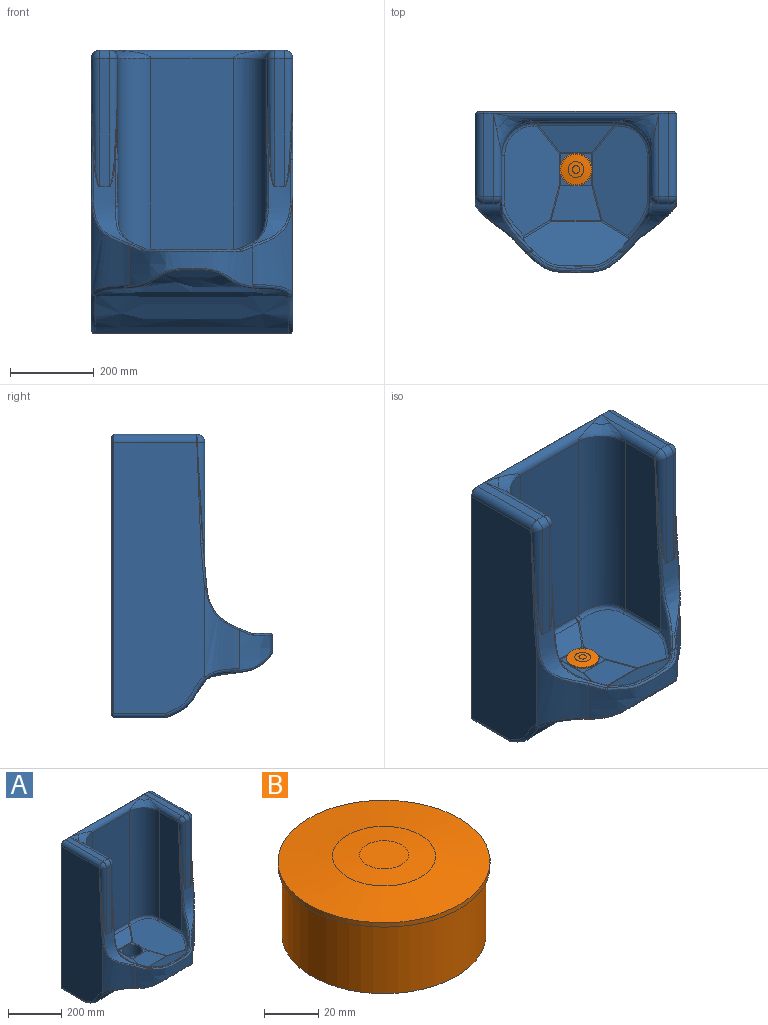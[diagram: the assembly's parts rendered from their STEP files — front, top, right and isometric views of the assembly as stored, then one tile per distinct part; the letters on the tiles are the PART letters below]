
ASSEMBLY  parts=2 mates=1
PART A: 140 faces, bbox 493.7x387.3x692.1 mm
  f0: bspline ~91.82x91.82mm, area 3088mm2, adj f69,f71,f137,f138
  f1: bspline ~91.82x91.82mm, area 3088mm2, adj f68,f69,f134,f135
  f2: plane 263.56x130.26mm, normal (0.24,0,0.97), area 28131.6mm2, adj f92,f97,f100,f101,f105,f106,f109,f110
  f3: plane 263.14x130.26mm, normal (-0.24,0,0.97), area 27983.2mm2, adj f85,f89,f90,f94,f95,f98,f99,f102
  f4: plane 199.28x23.5mm, normal (0,0,1), area 4683mm2, adj f71,f75,f80,f129
  f5: plane 463x125.22mm, normal (0,0,-1), area 57976mm2, adj f118,f120,f121,f130
  f6: plane 649.01x219.29mm, normal (1,0,0), area 134535.2mm2, adj f9,f33,f37,f80,f117,f118,f133
  f7: extruded ~308.32x96.53mm, area 21555.4mm2, adj f8,f9,f42,f45,f46,f47,f50,f116
  f8: extruded ~217.07x91.54mm, area 15555.5mm2, adj f7,f13,f34,f38,f42,f123,f124
  f9: extruded ~219.07x95.91mm, area 16070.7mm2, adj f6,f7,f37,f41,f45,f116,f117
  f10: plane 75.52x34.33mm, normal (0,0,1), area 647.8mm2, adj f81,f90,f91,f100
  f11: extruded ~215.89x127.47mm, area 8204.1mm2, adj f32,f36,f37,f40,f41,f45,f49,f53
  f12: extruded ~215.89x126.98mm, area 7962.1mm2, adj f31,f34,f35,f38,f39,f42,f48,f51
  f13: plane 649.01x219.29mm, normal (-1,0,0), area 134535.2mm2, adj f8,f30,f34,f59,f121,f123,f126
  f14: plane 228.61x44.47mm, normal (0,0,1), area 1469.2mm2, adj f46,f51,f54,f57
  f15: plane 305.81x23.5mm, normal (0,-1,0), area 7186.5mm2, adj f26,f29,f35,f63
  f16: plane 305.81x23.5mm, normal (0,-1,0), area 7186.5mm2, adj f27,f28,f36,f75
  f17: plane 199.28x23.5mm, normal (0,0,1), area 4683mm2, adj f59,f63,f68,f129
  f18: plane 489.87x121.03mm, normal (-1,0,0), area 54168.9mm2, adj f22,f44,f49,f53,f71,f94,f98,f138
  f19: plane 489.25x119.68mm, normal (1,0,0), area 54166.7mm2, adj f22,f43,f48,f52,f68,f101,f106,f135
  f20: plane 669x473mm, normal (0,1,0), area 316329.7mm2, adj f126,f127,f128,f129,f130,f131,f132,f133
  f21: plane 508.8x196.66mm, normal (0,-1,0), area 100045.2mm2, adj f69,f102,f110,f111,f135,f138
  f22: extruded ~356x149.3mm, area 21982mm2, adj f18,f19,f24,f25,f52,f53,f55,f56
  f23: plane 75.52x33.75mm, normal (0,0,1), area 603.7mm2, adj f81,f99,f108,f109
  f24: plane 58.7x1.71mm, normal (0,0,1), area 35.8mm2, adj f22,f25
  f25: plane 250.47x105.46mm, normal (0,0.38,0.92), area 21551.1mm2, adj f22,f24,f88,f89,f94,f97,f101
  f26: cylinder r=20mm len=305.81mm, axis (0,0,-1), area 4605.5mm2, adj f15,f39,f64
  f27: cylinder r=20mm len=305.81mm, axis (0,0,1), area 4605.5mm2, adj f16,f40,f74
  f28: cylinder r=20mm len=305.81mm, axis (0,0,-1), area 4605.5mm2, adj f16,f32,f76
  f29: cylinder r=20mm len=305.81mm, axis (0,0,-1), area 4605.5mm2, adj f15,f31,f62
  f30: bspline ~264.56x16.21mm, area 908mm2, adj f13,f31,f34,f58
  f31: bspline ~331.15x25.29mm, area 495.5mm2, adj f12,f29,f30,f35,f58,f61
  f32: bspline ~337.72x25.79mm, area 495.5mm2, adj f11,f28,f33,f36,f77,f78
  f33: bspline ~260.8x15.67mm, area 908mm2, adj f6,f32,f37,f78
  f34: bspline ~158.45x18.65mm, area 824.3mm2, adj f8,f12,f13,f30,f38
  f35: cylinder r=5mm len=23.5mm, axis (-1,0,0), area 9mm2, adj f12,f15,f31,f39
  f36: cylinder r=5mm len=23.5mm, axis (-1,0,0), area 9mm2, adj f11,f16,f32,f40
  f37: bspline ~158.45x18.65mm, area 816.4mm2, adj f6,f9,f11,f33,f41
  f38: bspline ~111.33x98.62mm, area 905.9mm2, adj f8,f12,f34,f42
  f39: bspline ~337.72x25.79mm, area 495.5mm2, adj f12,f26,f35,f43,f65,f66
  f40: bspline ~331.15x25.29mm, area 495.5mm2, adj f11,f27,f36,f44,f70,f73
  f41: bspline ~117.07x102.52mm, area 942.1mm2, adj f9,f11,f37,f45
  f42: bspline ~44.18x42.51mm, area 285mm2, adj f7,f8,f12,f38,f47
  f43: bspline ~260.8x15.67mm, area 908mm2, adj f19,f39,f48,f66
  f44: bspline ~264.56x16.21mm, area 908mm2, adj f18,f40,f49,f70
  f45: bspline ~36.85x35.74mm, area 249.6mm2, adj f7,f9,f11,f41,f50
  f46: bspline ~249.11x56.73mm, area 2046.6mm2, adj f7,f14,f47,f50
  f47: bspline ~9.78x7.46mm, area 30.9mm2, adj f7,f42,f46,f51
  f48: bspline ~158.45x18.65mm, area 888.5mm2, adj f12,f19,f43,f52
  f49: bspline ~164.91x19.87mm, area 921.5mm2, adj f11,f18,f44,f53
  f50: bspline ~8.68x6.37mm, area 30.5mm2, adj f7,f45,f46,f54
  f51: cylinder r=5mm len=12.19mm, axis (-1,0,0), area 15.3mm2, adj f12,f14,f47,f55
  f52: bspline ~114.61x109.5mm, area 1639.2mm2, adj f12,f19,f22,f48,f55
  f53: bspline ~118.24x108.37mm, area 1630.9mm2, adj f11,f18,f22,f49,f56
  f54: cylinder r=5mm len=12.03mm, axis (-1,0,0), area 15.1mm2, adj f11,f14,f50,f56
  f55: bspline ~9.45x8.77mm, area 35.7mm2, adj f22,f51,f52,f57
  f56: bspline ~9.76x8.9mm, area 35.1mm2, adj f22,f53,f54,f57
  f57: bspline ~221.15x47.02mm, area 1799.9mm2, adj f14,f22,f55,f56
  f58: bspline ~0.83x0.54mm, area 0mm2, adj f30,f31,f59,f60
  f59: cylinder r=20mm len=199.87mm, axis (0,-1,0), area 6271.7mm2, adj f13,f17,f58,f60,f127
  f60: bspline ~22.19x20mm, area 6mm2, adj f58,f59,f61
  f61: bspline ~20.23x20.22mm, area 5.5mm2, adj f31,f60,f62
  f62: sphere r=20mm, area 602.4mm2, adj f29,f61,f63
  f63: cylinder r=20mm len=23.5mm, axis (1,0,0), area 738.3mm2, adj f15,f17,f62,f64
  f64: sphere r=20mm, area 602.4mm2, adj f26,f63,f65
  f65: bspline ~20.23x20.22mm, area 5.5mm2, adj f39,f64,f67
  f66: bspline ~0.83x0.54mm, area 0mm2, adj f39,f43,f67,f68
  f67: bspline ~20x19.94mm, area 6mm2, adj f65,f66,f68
  f68: cylinder r=20mm len=199.87mm, axis (0,1,0), area 4277.6mm2, adj f1,f17,f19,f66,f67,f134
  f69: cylinder r=20mm len=396mm, axis (1,0,0), area 8884.5mm2, adj f0,f1,f21,f129,f134,f137
  f70: bspline ~0.83x0.54mm, area 0mm2, adj f40,f44,f71,f72
  f71: cylinder r=20mm len=199.87mm, axis (0,-1,0), area 4276.5mm2, adj f0,f4,f18,f70,f72,f137
  f72: bspline ~20.51x20mm, area 6mm2, adj f70,f71,f73
  f73: bspline ~20.23x20.22mm, area 5.5mm2, adj f40,f72,f74
  f74: sphere r=20mm, area 602.4mm2, adj f27,f73,f75
  f75: cylinder r=20mm len=23.5mm, axis (1,0,0), area 738.3mm2, adj f4,f16,f74,f76
  f76: sphere r=20mm, area 602.4mm2, adj f28,f75,f77
  f77: bspline ~20.23x20.22mm, area 5.5mm2, adj f32,f76,f79
  f78: bspline ~0.83x0.54mm, area 0mm2, adj f32,f33,f79,f80
  f79: bspline ~20x19.94mm, area 6mm2, adj f77,f78,f80
  f80: cylinder r=20mm len=199.87mm, axis (0,1,0), area 6271.7mm2, adj f4,f6,f78,f79,f131
  f81: cylinder r=38mm len=89mm, axis (0,0,1), area 21249.7mm2, adj f10,f23,f82,f95,f105
  f82: plane 76x76mm, normal (0,0,1), area 4536.5mm2, adj f81
  f83: plane 120.02x82.89mm, normal (0,0.07,1), area 8122.4mm2, adj f85,f88,f91,f92
  f84: plane 180.35x65.99mm, normal (0,-0.2,0.98), area 8609.7mm2, adj f103,f108,f111,f114
  f85: cylinder r=10mm len=83.56mm, axis (0.26,-0.96,0.07), area 219.8mm2, adj f3,f83,f86,f87
  f86: sphere r=10mm, area 4.2mm2, adj f85,f88,f89
  f87: sphere r=10mm, area 0.8mm2, adj f85,f90,f91
  f88: cylinder r=10mm len=120.02mm, axis (1,0,0), area 389.9mm2, adj f25,f83,f86,f93
  f89: cylinder r=10mm len=67.34mm, axis (-0.84,0.51,-0.21), area 349.1mm2, adj f3,f25,f86,f94
  f90: cylinder r=10mm len=34.33mm, axis (0,1,0), area 84.7mm2, adj f3,f10,f87,f95
  f91: cylinder r=10mm len=75.52mm, axis (-1,0,0), area 51mm2, adj f10,f83,f87,f96
  f92: cylinder r=10mm len=83.56mm, axis (-0.26,-0.96,0.07), area 219.8mm2, adj f2,f83,f93,f96
  f93: sphere r=10mm, area 5.9mm2, adj f88,f92,f97
  f94: bspline ~103.82x71.12mm, area 1368.3mm2, adj f3,f18,f22,f25,f89,f98
  f95: bspline ~14.43x2.89mm, area 19.6mm2, adj f3,f81,f90,f99
  f96: sphere r=10mm, area 0.7mm2, adj f91,f92,f100
  f97: cylinder r=10mm len=67.98mm, axis (0.84,0.51,-0.21), area 352.8mm2, adj f2,f25,f93,f101
  f98: cylinder r=10mm len=119.6mm, axis (0,1,0), area 1573.3mm2, adj f3,f18,f94,f139
  f99: cylinder r=10mm len=33.75mm, axis (0,1,0), area 83.2mm2, adj f3,f23,f95,f104
  f100: cylinder r=10mm len=34.33mm, axis (0,1,0), area 84.7mm2, adj f2,f10,f96,f105
  f101: bspline ~96.29x66.51mm, area 1374.6mm2, adj f2,f19,f22,f25,f97,f106
  f102: cylinder r=10mm len=11.75mm, axis (0.97,0,0.24), area 132.1mm2, adj f3,f21,f107,f139
  f103: cylinder r=10mm len=67.95mm, axis (-0.61,-0.77,-0.15), area 268.4mm2, adj f3,f84,f104,f107
  f104: sphere r=10mm, area 3.5mm2, adj f99,f103,f108
  f105: bspline ~14.43x2.89mm, area 19.6mm2, adj f2,f81,f100,f109
  f106: cylinder r=10mm len=119.61mm, axis (0,-1,0), area 1583.2mm2, adj f2,f19,f101,f136
  f107: sphere r=10mm, area 22.2mm2, adj f102,f103,f111
  f108: cylinder r=10mm len=75.52mm, axis (1,0,0), area 149.1mm2, adj f23,f84,f104,f112
  f109: cylinder r=10mm len=33.75mm, axis (0,1,0), area 83.2mm2, adj f2,f23,f105,f112
  f110: cylinder r=10mm len=11.75mm, axis (-0.97,0,0.24), area 132.1mm2, adj f2,f21,f113,f136
  f111: cylinder r=10mm len=180.35mm, axis (-1,0,0), area 2476.9mm2, adj f21,f84,f107,f113
  f112: sphere r=10mm, area 4.9mm2, adj f108,f109,f114
  f113: sphere r=10mm, area 20.8mm2, adj f110,f111,f114
  f114: cylinder r=10mm len=67.95mm, axis (0.61,-0.77,-0.15), area 268.4mm2, adj f2,f84,f112,f113
  f115: extruded ~463x251.48mm, area 110946.3mm2, adj f116,f117,f120,f123,f124,f125
  f116: bspline ~103.26x86.67mm, area 1608.6mm2, adj f7,f9,f115,f117,f125
  f117: bspline ~106.41x104.43mm, area 2110.1mm2, adj f6,f9,f115,f116,f119
  f118: cylinder r=10mm len=125.22mm, axis (0,-1,0), area 1966.9mm2, adj f5,f6,f119,f132
  f119: sphere r=10mm, area 39.9mm2, adj f117,f118,f120
  f120: cylinder r=10mm len=463mm, axis (-1,0,0), area 1845.9mm2, adj f5,f115,f119,f122
  f121: cylinder r=10mm len=125.22mm, axis (0,1,0), area 1966.9mm2, adj f5,f13,f122,f128
  f122: sphere r=10mm, area 39.9mm2, adj f120,f121,f123
  f123: bspline ~106.41x104.43mm, area 2113.5mm2, adj f8,f13,f115,f122,f124
  f124: bspline ~100.9x84.96mm, area 1495.3mm2, adj f7,f8,f115,f123,f125
  f125: bspline ~332.29x107.74mm, area 2134.5mm2, adj f7,f115,f116,f124
  f126: plane 649x5mm, normal (-0.71,0.71,0), area 4589.1mm2, adj f13,f20,f127,f128
  f127: cone r=15mm half-angle=45deg, axis (0,-1,0), area 194.4mm2, adj f20,f59,f126,f129
  f128: cone r=5mm half-angle=45deg, axis (0,-1,0), area 83.3mm2, adj f20,f121,f126,f130
  f129: plane 443x5mm, normal (0,0.71,0.71), area 3132.5mm2, adj f4,f17,f20,f69,f127,f131
  f130: plane 463x5mm, normal (0,0.71,-0.71), area 3273.9mm2, adj f5,f20,f128,f132
  f131: cone r=15mm half-angle=45deg, axis (0,-1,0), area 194.4mm2, adj f20,f80,f129,f133
  f132: cone r=5mm half-angle=45deg, axis (0,-1,0), area 83.3mm2, adj f20,f118,f130,f133
  f133: plane 649x5mm, normal (0.71,0.71,0), area 4589.1mm2, adj f6,f20,f131,f132
  f134: bspline ~39.28x39.13mm, area 483.7mm2, adj f1,f68,f69
  f135: cylinder r=79.67mm len=506.75mm, axis (0,0,1), area 62318.8mm2, adj f1,f19,f21,f136
  f136: bspline ~79.67x79.67mm, area 1705.3mm2, adj f2,f106,f110,f135
  f137: bspline ~39.28x39.13mm, area 483.7mm2, adj f0,f69,f71
  f138: cylinder r=79.67mm len=506.75mm, axis (0,0,-1), area 62318.8mm2, adj f0,f18,f21,f139
  f139: bspline ~79.67x79.67mm, area 1705.3mm2, adj f3,f98,f102,f138
PART B: 11 faces, bbox 78x78x36 mm
  f0: cylinder r=35mm len=70mm, axis (0,0,-1), area 6597.3mm2, adj f3,f5
  f1: cylinder r=37.5mm len=75mm, axis (0,0,-1), area 7068.6mm2, adj f2,f3
  f2: plane 75x75mm, normal (0,0,1), area 232.5mm2, adj f1,f4
  f3: plane 75x75mm, normal (0,0,-1), area 569.4mm2, adj f0,f1
  f4: cylinder r=36.5mm len=73mm, axis (0,0,-1), area 229.3mm2, adj f2,f8
  f5: plane 70x70mm, normal (0,0,-1), area 3848.5mm2, adj f0
  f6: cylinder r=39mm len=78mm, axis (0,0,-1), area 490.1mm2, adj f8,f9
  f7: plane 18x18mm, normal (0,0,1), area 254.5mm2, adj f10
  f8: plane 78x78mm, normal (0,0,-1), area 593mm2, adj f4,f6
  f9: cone r=14mm half-angle=83.2deg, axis (0,0,-1), area 3674.7mm2, adj f6,f10
  f10: cone r=9mm half-angle=86.6deg, axis (0,0,-1), area 877mm2, adj f7,f9
PLACE A t=(-412.16,-168.38,159)mm fixed
PLACE B t=(-412.16,-282.38,-81.5)mm
MATE slider A.f81 <-> B.f0  axis (0,0,1) through (-412.16,-282.38,-53.5)mm
